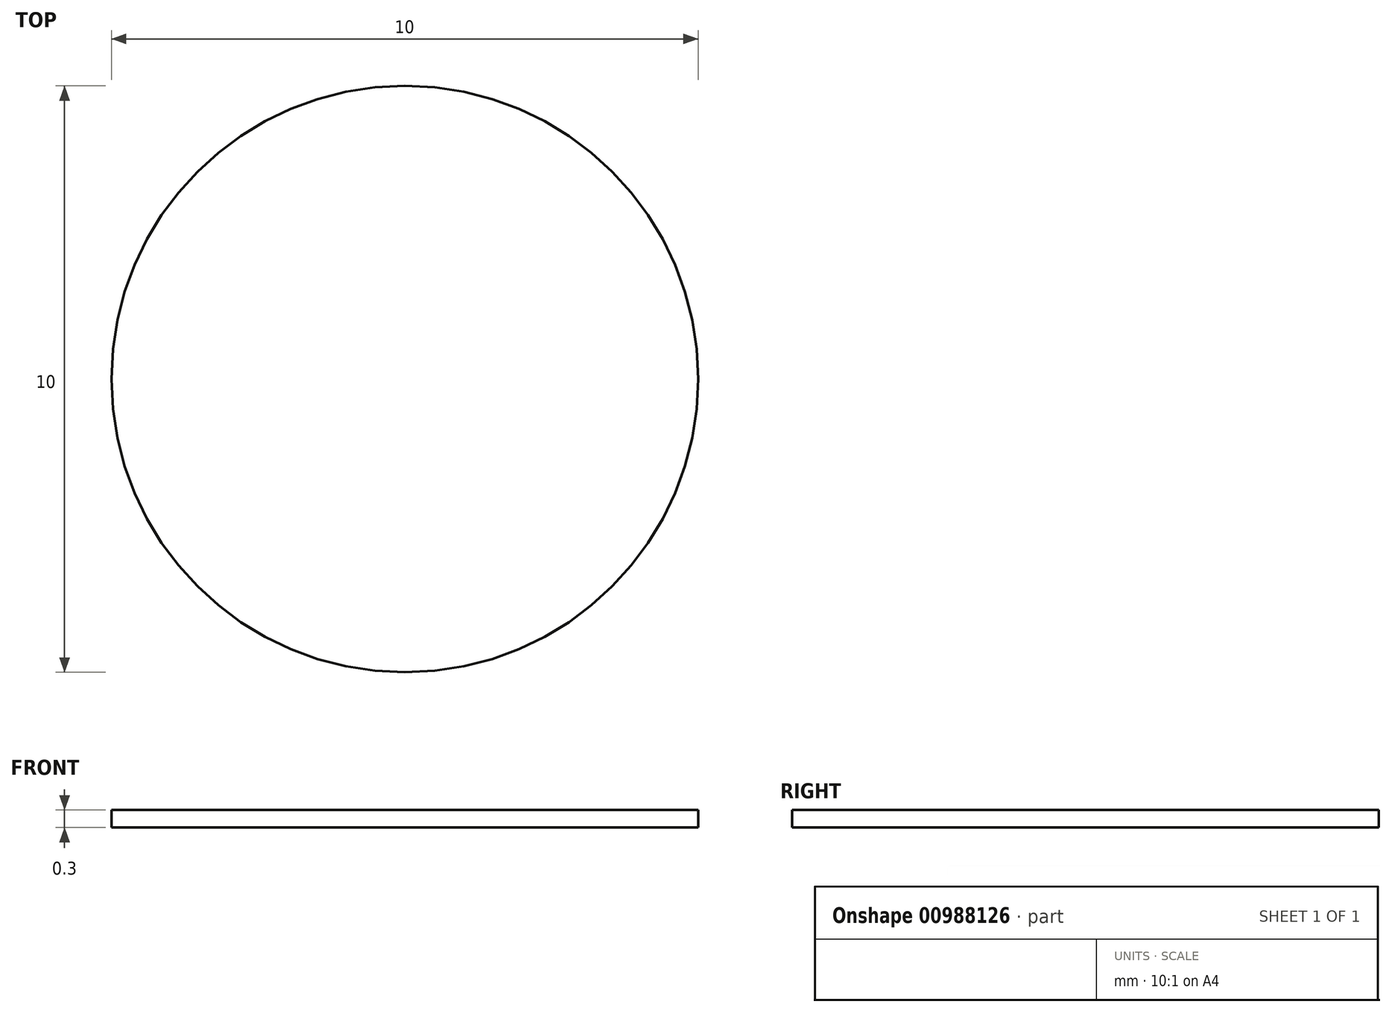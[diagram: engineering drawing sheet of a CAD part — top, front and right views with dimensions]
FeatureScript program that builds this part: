
annotation { "Feature Type Name" : "Feature", "Feature Type Description" : "" }
export const myFeature = defineFeature(function(context is Context, id is Id, definition is map)
    precondition{}
    {
        {
            var Q0;
            Q0=qCreatedBy(makeId("Top.planeOp"),FACE);
            var sketch = newSketch(context, id + "F0", { "sketchPlane" : qUnion([Q0])});
            skCircle(sketch, "E0", {"center": v(0, 0) * mm, "radius": 5 * mm});
            skSolve(sketch);
        }
        {
            var Q0;
            Q0 = qSketchRegion(id + "F0", true);
            extrude(context, id + "F1", {"entities" : qUnion([Q0]), "depth" : 0.3 * mm, "offsetDistance" : 25 * mm});
        }
    });
